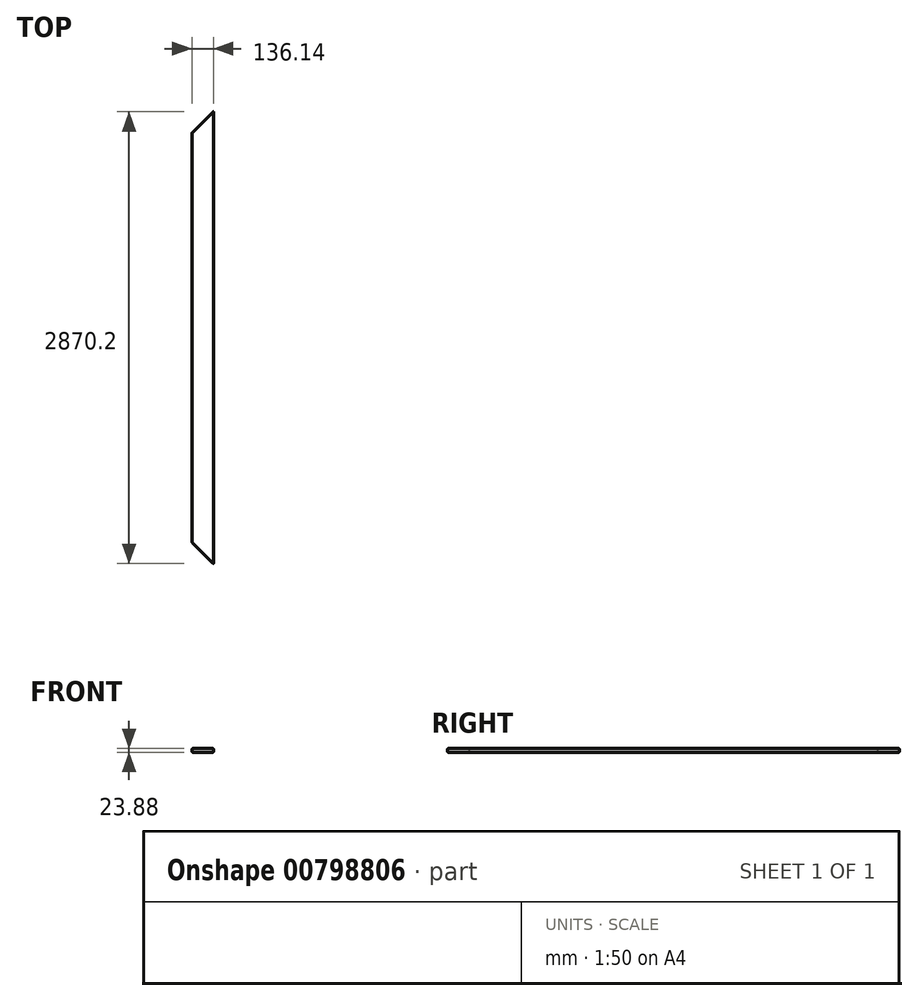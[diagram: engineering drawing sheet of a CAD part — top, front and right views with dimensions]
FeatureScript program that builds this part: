
annotation { "Feature Type Name" : "Feature", "Feature Type Description" : "" }
export const myFeature = defineFeature(function(context is Context, id is Id, definition is map)
    precondition{}
    {
        {
            var Q0;
            Q0=qCreatedBy(makeId("Front.planeOp"),FACE);
            var sketch = newSketch(context, id + "F0", { "sketchPlane" : qUnion([Q0])});
            skLineSegment(sketch, "E0.bottom", {"start": v(-63.25, 11.94) * mm, "end": v(63.25, 11.94) * mm});
            skLineSegment(sketch, "E0.top", {"start": v(-63.25, -11.94) * mm, "end": v(63.25, -11.94) * mm});
            skLineSegment(sketch, "E0.left", {"start": v(-68.07, 7.11) * mm, "end": v(-68.07, -7.11) * mm});
            skLineSegment(sketch, "E0.right", {"start": v(68.07, 7.11) * mm, "end": v(68.07, -7.11) * mm});
            skPoint(sketch, "E0.middle", {"position": v(0, 0) * mm});
            skPoint(sketch, "E1.visualSharp", {"position": v(-68.07, 11.94) * mm});
            skArc(sketch, "E1.filletArc", {"start": v(-63.25, 11.94) * mm, "mid": v(-66.66, 10.52) * mm, "end": v(-68.07, 7.11) * mm});
            skPoint(sketch, "E2.visualSharp", {"position": v(68.07, 11.94) * mm});
            skArc(sketch, "E2.filletArc", {"start": v(68.07, 7.11) * mm, "mid": v(66.66, 10.52) * mm, "end": v(63.25, 11.94) * mm});
            skPoint(sketch, "E3.visualSharp", {"position": v(68.07, -11.94) * mm});
            skArc(sketch, "E3.filletArc", {"start": v(63.25, -11.94) * mm, "mid": v(66.66, -10.52) * mm, "end": v(68.07, -7.11) * mm});
            skPoint(sketch, "E4.visualSharp", {"position": v(-68.07, -11.94) * mm});
            skArc(sketch, "E4.filletArc", {"start": v(-68.07, -7.11) * mm, "mid": v(-66.66, -10.52) * mm, "end": v(-63.25, -11.94) * mm});
            skSolve(sketch);
        }
        {
            var Q0;
            Q0=makeQuery(id+"F0.imprint","IMPRINT",FACE,{"disambiguationData":[TD([[makeQuery(id+"F0.imprint","IMPRINT",EDGE,{"derivedFrom":sQuery(id+"F0.wireOp",EDGE,"E0.bottom")}),-1.0]])]});
            extrude(context, id + "F1", {"entities" : qUnion([Q0]), "endBound" : BoundingType.SYMMETRIC, "depth" : 2870.2 * mm, "offsetDistance" : 25.4 * mm});
        }
        {
            var Q0;
            Q0=makeQuery(id+"F1.opExtrude","SWEPT_FACE",FACE,{"disambiguationData":[OSD([sQuery(id+"F0.wireOp",EDGE,"E0.bottom")])]});
            var sketch = newSketch(context, id + "F2", { "sketchPlane" : qUnion([Q0])});
            skLineSegment(sketch, "E5", {"start": v(-68.07, 1435.1) * mm, "end": v(68.07, 1435.1) * mm});
            skLineSegment(sketch, "E6", {"start": v(-68.07, 1435.1) * mm, "end": v(-68.07, 1298.96) * mm});
            skLineSegment(sketch, "E7", {"start": v(-68.07, 1298.96) * mm, "end": v(68.07, 1435.1) * mm});
            skSolve(sketch);
        }
        {
            var Q0;
            Q0 = qSketchRegion(id + "F2", true);
            extrude(context, id + "F3", {"entities" : qUnion([Q0]), "operationType" : NewBodyOperationType.REMOVE, "endBound" : BoundingType.THROUGH_ALL, "oppositeDirection" : true, "depth" : 25.4 * mm, "offsetDistance" : 25.4 * mm});
        }
        {
            var Q0;
            Q0=makeQuery(id+"F1.opExtrude","SWEPT_FACE",FACE,{"disambiguationData":[OSD([sQuery(id+"F0.wireOp",EDGE,"E0.top")])]});
            var sketch = newSketch(context, id + "F4", { "sketchPlane" : qUnion([Q0])});
            skLineSegment(sketch, "E8", {"start": v(-68.07, 1435.1) * mm, "end": v(68.07, 1435.1) * mm});
            skLineSegment(sketch, "E9", {"start": v(-68.07, 1435.1) * mm, "end": v(-68.07, 1298.96) * mm});
            skLineSegment(sketch, "E10", {"start": v(-68.07, 1298.96) * mm, "end": v(68.07, 1435.1) * mm});
            skSolve(sketch);
        }
        {
            var Q0;
            Q0 = qSketchRegion(id + "F4", true);
            extrude(context, id + "F5", {"entities" : qUnion([Q0]), "operationType" : NewBodyOperationType.REMOVE, "endBound" : BoundingType.THROUGH_ALL, "oppositeDirection" : true, "depth" : 25.4 * mm, "offsetDistance" : 25.4 * mm});
        }
    });
